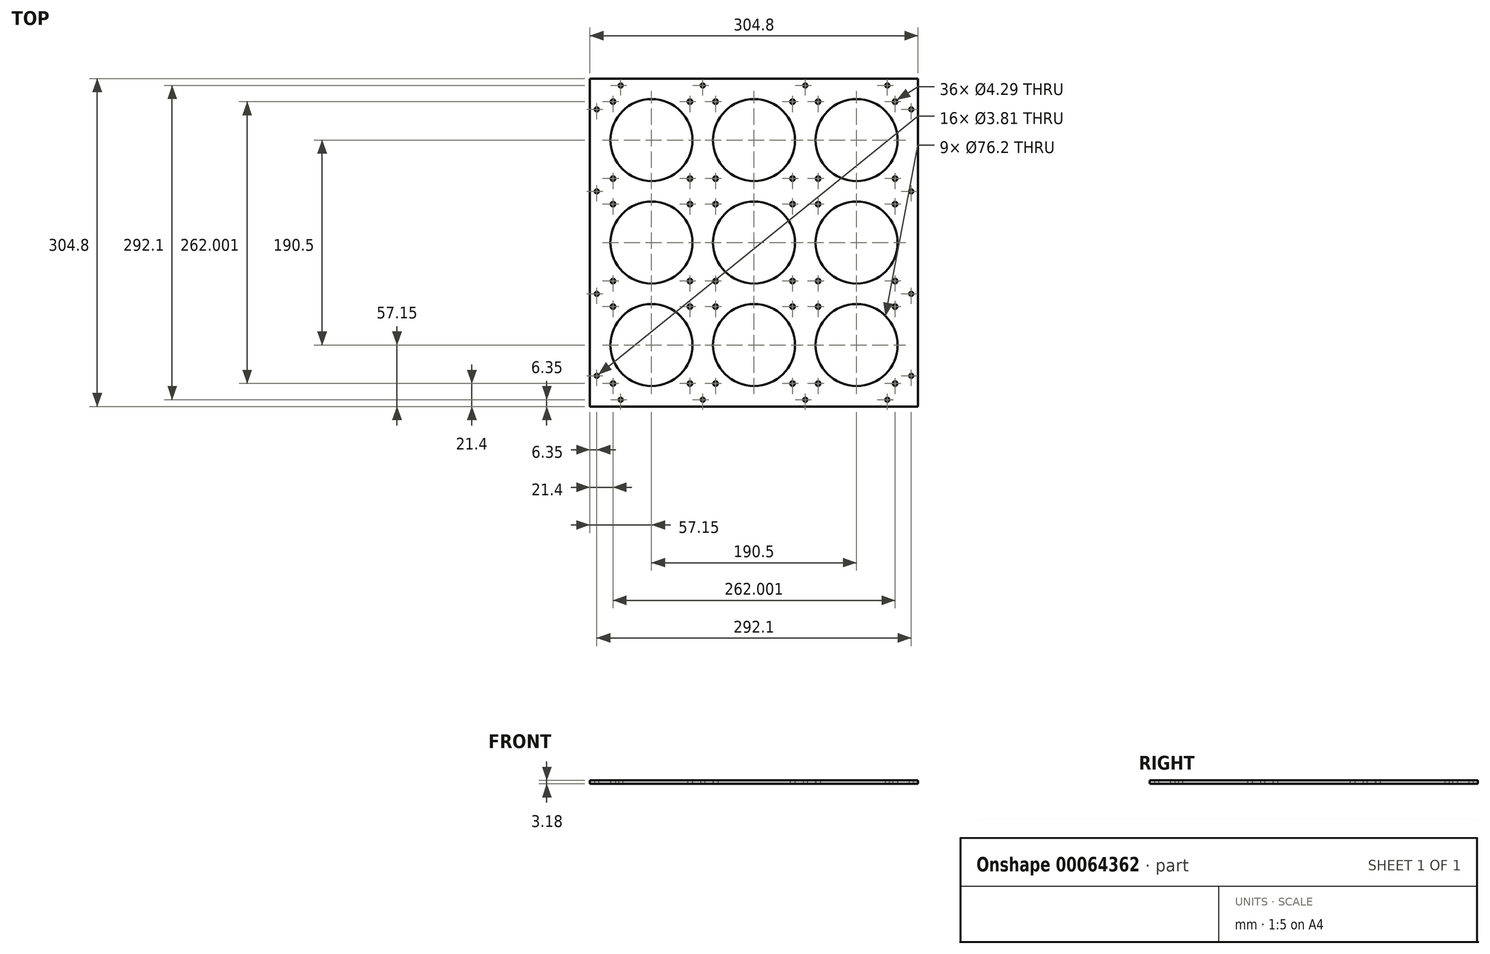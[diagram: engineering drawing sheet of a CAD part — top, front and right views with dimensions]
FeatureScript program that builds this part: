
annotation { "Feature Type Name" : "Feature", "Feature Type Description" : "" }
export const myFeature = defineFeature(function(context is Context, id is Id, definition is map)
    precondition{}
    {
        {
            var Q0;
            Q0=qCreatedBy(makeId("Top.planeOp"),FACE);
            var sketch = newSketch(context, id + "F0", { "sketchPlane" : qUnion([Q0])});
            skLineSegment(sketch, "E0.rect.bottom", {"start": v(-152.4, 152.4) * mm, "end": v(152.4, 152.4) * mm});
            skLineSegment(sketch, "E0.rect.top", {"start": v(-152.4, -152.4) * mm, "end": v(152.4, -152.4) * mm});
            skLineSegment(sketch, "E0.rect.left", {"start": v(-152.4, 152.4) * mm, "end": v(-152.4, -152.4) * mm});
            skLineSegment(sketch, "E0.rect.right", {"start": v(152.4, 152.4) * mm, "end": v(152.4, -152.4) * mm});
            skPoint(sketch, "E1", {"position": v(-47.62, 146.05) * mm});
            skPoint(sketch, "E2", {"position": v(47.63, 146.05) * mm});
            skPoint(sketch, "E3", {"position": v(-47.62, -146.05) * mm});
            skPoint(sketch, "E4", {"position": v(47.63, -146.05) * mm});
            skPoint(sketch, "E5", {"position": v(-146.05, 47.63) * mm});
            skPoint(sketch, "E6", {"position": v(-146.05, -47.62) * mm});
            skPoint(sketch, "E7", {"position": v(146.05, 47.63) * mm});
            skPoint(sketch, "E8", {"position": v(-123.83, 146.05) * mm});
            skPoint(sketch, "E9", {"position": v(-146.05, 123.83) * mm});
            skPoint(sketch, "E10", {"position": v(123.83, 146.05) * mm});
            skPoint(sketch, "E11", {"position": v(-146.05, -123.82) * mm});
            skPoint(sketch, "E12", {"position": v(-123.83, -146.05) * mm});
            skPoint(sketch, "E13", {"position": v(123.83, -146.05) * mm});
            skPoint(sketch, "E14", {"position": v(146.05, -123.82) * mm});
            skPoint(sketch, "E15", {"position": v(146.05, 123.83) * mm});
            skPoint(sketch, "E16", {"position": v(146.05, -47.62) * mm});
            skPoint(sketch, "E17.rect.middle", {"position": v(0, 0) * mm});
            skCircle(sketch, "E18", {"center": v(-95.25, 95.25) * mm, "radius": 38.1 * mm});
            skCircle(sketch, "E19", {"center": v(-131, 131) * mm, "radius": 2.15 * mm});
            skCircle(sketch, "E20.0.1.0", {"center": v(-131, 59.5) * mm, "radius": 2.15 * mm});
            skCircle(sketch, "E20.1.0.0", {"center": v(-59.5, 131) * mm, "radius": 2.15 * mm});
            skCircle(sketch, "E20.1.1.0", {"center": v(-59.5, 59.5) * mm, "radius": 2.15 * mm});
            skLineSegment(sketch, "E20.direction1", {"start": v(-131, 131) * mm, "end": v(-59.5, 131) * mm, "construction": true});
            skLineSegment(sketch, "E20.direction2", {"start": v(-131, 131) * mm, "end": v(-131, 59.5) * mm, "construction": true});
            skLineSegment(sketch, "E21.0.1.0", {"start": v(-131, 35.75) * mm, "end": v(-59.5, 35.75) * mm, "construction": true});
            skLineSegment(sketch, "E21.0.1.1", {"start": v(-131, 35.75) * mm, "end": v(-131, -35.75) * mm, "construction": true});
            skCircle(sketch, "E21.0.1.2", {"center": v(-95.25, 0) * mm, "radius": 38.1 * mm});
            skPoint(sketch, "E21.0.1.3", {"position": v(-95.25, 0) * mm});
            skCircle(sketch, "E21.0.1.4", {"center": v(-59.5, -35.75) * mm, "radius": 2.15 * mm});
            skCircle(sketch, "E21.0.1.5", {"center": v(-131, -35.75) * mm, "radius": 2.15 * mm});
            skCircle(sketch, "E21.0.1.6", {"center": v(-59.5, 35.75) * mm, "radius": 2.15 * mm});
            skCircle(sketch, "E21.0.1.7", {"center": v(-131, 35.75) * mm, "radius": 2.15 * mm});
            skLineSegment(sketch, "E21.1.0.0", {"start": v(-35.75, 131) * mm, "end": v(35.75, 131) * mm, "construction": true});
            skLineSegment(sketch, "E21.1.0.1", {"start": v(-35.75, 131) * mm, "end": v(-35.75, 59.5) * mm, "construction": true});
            skCircle(sketch, "E21.1.0.2", {"center": v(0, 95.25) * mm, "radius": 38.1 * mm});
            skPoint(sketch, "E21.1.0.3", {"position": v(0, 95.25) * mm});
            skCircle(sketch, "E21.1.0.4", {"center": v(35.75, 59.5) * mm, "radius": 2.15 * mm});
            skCircle(sketch, "E21.1.0.5", {"center": v(-35.75, 59.5) * mm, "radius": 2.15 * mm});
            skCircle(sketch, "E21.1.0.6", {"center": v(35.75, 131) * mm, "radius": 2.15 * mm});
            skCircle(sketch, "E21.1.0.7", {"center": v(-35.75, 131) * mm, "radius": 2.15 * mm});
            skLineSegment(sketch, "E21.1.1.0", {"start": v(-35.75, 35.75) * mm, "end": v(35.75, 35.75) * mm, "construction": true});
            skLineSegment(sketch, "E21.1.1.1", {"start": v(-35.75, 35.75) * mm, "end": v(-35.75, -35.75) * mm, "construction": true});
            skCircle(sketch, "E21.1.1.2", {"center": v(0, 0) * mm, "radius": 38.1 * mm});
            skCircle(sketch, "E21.1.1.4", {"center": v(35.75, -35.75) * mm, "radius": 2.15 * mm});
            skCircle(sketch, "E21.1.1.5", {"center": v(-35.75, -35.75) * mm, "radius": 2.15 * mm});
            skCircle(sketch, "E21.1.1.6", {"center": v(35.75, 35.75) * mm, "radius": 2.15 * mm});
            skCircle(sketch, "E21.1.1.7", {"center": v(-35.75, 35.75) * mm, "radius": 2.15 * mm});
            skLineSegment(sketch, "E21.2.0.0", {"start": v(59.5, 131) * mm, "end": v(131, 131) * mm, "construction": true});
            skLineSegment(sketch, "E21.2.0.1", {"start": v(59.5, 131) * mm, "end": v(59.5, 59.5) * mm, "construction": true});
            skCircle(sketch, "E21.2.0.2", {"center": v(95.25, 95.25) * mm, "radius": 38.1 * mm});
            skPoint(sketch, "E21.2.0.3", {"position": v(95.25, 95.25) * mm});
            skCircle(sketch, "E21.2.0.4", {"center": v(131, 59.5) * mm, "radius": 2.15 * mm});
            skCircle(sketch, "E21.2.0.5", {"center": v(59.5, 59.5) * mm, "radius": 2.15 * mm});
            skCircle(sketch, "E21.2.0.6", {"center": v(131, 131) * mm, "radius": 2.15 * mm});
            skCircle(sketch, "E21.2.0.7", {"center": v(59.5, 131) * mm, "radius": 2.15 * mm});
            skLineSegment(sketch, "E21.2.1.0", {"start": v(59.5, 35.75) * mm, "end": v(131, 35.75) * mm, "construction": true});
            skLineSegment(sketch, "E21.2.1.1", {"start": v(59.5, 35.75) * mm, "end": v(59.5, -35.75) * mm, "construction": true});
            skCircle(sketch, "E21.2.1.2", {"center": v(95.25, 0) * mm, "radius": 38.1 * mm});
            skPoint(sketch, "E21.2.1.3", {"position": v(95.25, 0) * mm});
            skCircle(sketch, "E21.2.1.4", {"center": v(131, -35.75) * mm, "radius": 2.15 * mm});
            skCircle(sketch, "E21.2.1.5", {"center": v(59.5, -35.75) * mm, "radius": 2.15 * mm});
            skCircle(sketch, "E21.2.1.6", {"center": v(131, 35.75) * mm, "radius": 2.15 * mm});
            skCircle(sketch, "E21.2.1.7", {"center": v(59.5, 35.75) * mm, "radius": 2.15 * mm});
            skLineSegment(sketch, "E21.direction1", {"start": v(-131, 131) * mm, "end": v(-35.75, 131) * mm, "construction": true});
            skLineSegment(sketch, "E21.direction2", {"start": v(-131, 131) * mm, "end": v(-131, 35.75) * mm, "construction": true});
            skLineSegment(sketch, "E22.0.0.2", {"start": v(-131, -59.5) * mm, "end": v(-59.5, -59.5) * mm, "construction": true});
            skLineSegment(sketch, "E22.3.0.2", {"start": v(-131, -59.5) * mm, "end": v(-131, -131) * mm, "construction": true});
            skCircle(sketch, "E22.6.0.2", {"center": v(-95.25, -95.25) * mm, "radius": 38.1 * mm});
            skPoint(sketch, "E22.8.0.2", {"position": v(-95.25, -95.25) * mm});
            skCircle(sketch, "E22.9.0.2", {"center": v(-59.5, -131) * mm, "radius": 2.15 * mm});
            skCircle(sketch, "E22.11.0.2", {"center": v(-131, -131) * mm, "radius": 2.15 * mm});
            skCircle(sketch, "E22.13.0.2", {"center": v(-59.5, -59.5) * mm, "radius": 2.15 * mm});
            skCircle(sketch, "E22.15.0.2", {"center": v(-131, -59.5) * mm, "radius": 2.15 * mm});
            skLineSegment(sketch, "E22.0.1.2", {"start": v(-35.75, -59.5) * mm, "end": v(35.75, -59.5) * mm, "construction": true});
            skLineSegment(sketch, "E22.3.1.2", {"start": v(-35.75, -59.5) * mm, "end": v(-35.75, -131) * mm, "construction": true});
            skCircle(sketch, "E22.6.1.2", {"center": v(0, -95.25) * mm, "radius": 38.1 * mm});
            skPoint(sketch, "E22.8.1.2", {"position": v(0, -95.25) * mm});
            skCircle(sketch, "E22.9.1.2", {"center": v(35.75, -131) * mm, "radius": 2.15 * mm});
            skCircle(sketch, "E22.11.1.2", {"center": v(-35.75, -131) * mm, "radius": 2.15 * mm});
            skCircle(sketch, "E22.13.1.2", {"center": v(35.75, -59.5) * mm, "radius": 2.15 * mm});
            skCircle(sketch, "E22.15.1.2", {"center": v(-35.75, -59.5) * mm, "radius": 2.15 * mm});
            skLineSegment(sketch, "E22.0.2.2", {"start": v(59.5, -59.5) * mm, "end": v(131, -59.5) * mm, "construction": true});
            skLineSegment(sketch, "E22.3.2.2", {"start": v(59.5, -59.5) * mm, "end": v(59.5, -131) * mm, "construction": true});
            skCircle(sketch, "E22.6.2.2", {"center": v(95.25, -95.25) * mm, "radius": 38.1 * mm});
            skPoint(sketch, "E22.8.2.2", {"position": v(95.25, -95.25) * mm});
            skCircle(sketch, "E22.9.2.2", {"center": v(131, -131) * mm, "radius": 2.15 * mm});
            skCircle(sketch, "E22.11.2.2", {"center": v(59.5, -131) * mm, "radius": 2.15 * mm});
            skCircle(sketch, "E22.13.2.2", {"center": v(131, -59.5) * mm, "radius": 2.15 * mm});
            skCircle(sketch, "E22.15.2.2", {"center": v(59.5, -59.5) * mm, "radius": 2.15 * mm});
            skSolve(sketch);
        }
        {
            var Q0;
            Q0=qSketchRegion(id+"F0",true);
            extrude(context, id + "F1", {"entities" : qUnion([Q0]), "depth" : 3.17 * mm});
        }
        {
            var Q0;
            Q0=sQuery(id+"F0.wireOp",VERTEX,"E9");
            var Q1;
            Q1=sQuery(id+"F0.wireOp",VERTEX,"E8");
            var Q2;
            Q2=sQuery(id+"F0.wireOp",VERTEX,"E10");
            var Q3;
            Q3=sQuery(id+"F0.wireOp",VERTEX,"E14");
            var Q4;
            Q4=sQuery(id+"F0.wireOp",VERTEX,"E13");
            var Q5;
            Q5=sQuery(id+"F0.wireOp",VERTEX,"E11");
            var Q6;
            Q6=sQuery(id+"F0.wireOp",VERTEX,"E12");
            var Q7;
            Q7=sQuery(id+"F0.wireOp",VERTEX,"E5");
            var Q8;
            Q8=sQuery(id+"F0.wireOp",VERTEX,"E6");
            var Q9;
            Q9=sQuery(id+"F0.wireOp",VERTEX,"E3");
            var Q10;
            Q10=sQuery(id+"F0.wireOp",VERTEX,"E4");
            var Q11;
            Q11=sQuery(id+"F0.wireOp",VERTEX,"E16");
            var Q12;
            Q12=sQuery(id+"F0.wireOp",VERTEX,"E7");
            var Q13;
            Q13=sQuery(id+"F0.wireOp",VERTEX,"E2");
            var Q14;
            Q14=sQuery(id+"F0.wireOp",VERTEX,"E1");
            var Q15;
            Q15=sQuery(id+"F0.wireOp",VERTEX,"E15");
            var Q16;
            Q16=makeQuery(id+"F1.opExtrude","SWEPT_BODY",BODY,{"disambiguationData":[OSD([sQuery(id+"F0.wireOp",EDGE,"E0.rect.bottom"),sQuery(id+"F0.wireOp",EDGE,"E0.rect.top"),sQuery(id+"F0.wireOp",EDGE,"E0.rect.left"),sQuery(id+"F0.wireOp",EDGE,"E0.rect.right"),sQuery(id+"F0.wireOp",EDGE,"355e2ae6-6e88-4ca4-8ebc-3fd0fd05b8a7"),sQuery(id+"F0.wireOp",EDGE,"ec92c217-216e-4417-a66e-f22207dcd941.0.1.0"),sQuery(id+"F0.wireOp",EDGE,"ec92c217-216e-4417-a66e-f22207dcd941.1.0.0"),sQuery(id+"F0.wireOp",EDGE,"ec92c217-216e-4417-a66e-f22207dcd941.1.1.0"),sQuery(id+"F0.wireOp",EDGE,"73b4038f-2a48-4c89-9a6c-eaebf8faa2ab.0.1.4"),sQuery(id+"F0.wireOp",EDGE,"73b4038f-2a48-4c89-9a6c-eaebf8faa2ab.0.1.5"),sQuery(id+"F0.wireOp",EDGE,"73b4038f-2a48-4c89-9a6c-eaebf8faa2ab.0.1.6"),sQuery(id+"F0.wireOp",EDGE,"73b4038f-2a48-4c89-9a6c-eaebf8faa2ab.0.1.7"),sQuery(id+"F0.wireOp",EDGE,"73b4038f-2a48-4c89-9a6c-eaebf8faa2ab.0.2.4"),sQuery(id+"F0.wireOp",EDGE,"73b4038f-2a48-4c89-9a6c-eaebf8faa2ab.0.2.5"),sQuery(id+"F0.wireOp",EDGE,"73b4038f-2a48-4c89-9a6c-eaebf8faa2ab.0.2.6"),sQuery(id+"F0.wireOp",EDGE,"73b4038f-2a48-4c89-9a6c-eaebf8faa2ab.0.2.7"),sQuery(id+"F0.wireOp",EDGE,"73b4038f-2a48-4c89-9a6c-eaebf8faa2ab.1.0.4"),sQuery(id+"F0.wireOp",EDGE,"73b4038f-2a48-4c89-9a6c-eaebf8faa2ab.1.0.5"),sQuery(id+"F0.wireOp",EDGE,"73b4038f-2a48-4c89-9a6c-eaebf8faa2ab.1.0.6"),sQuery(id+"F0.wireOp",EDGE,"73b4038f-2a48-4c89-9a6c-eaebf8faa2ab.1.0.7"),sQuery(id+"F0.wireOp",EDGE,"73b4038f-2a48-4c89-9a6c-eaebf8faa2ab.1.1.4"),sQuery(id+"F0.wireOp",EDGE,"73b4038f-2a48-4c89-9a6c-eaebf8faa2ab.1.1.5"),sQuery(id+"F0.wireOp",EDGE,"73b4038f-2a48-4c89-9a6c-eaebf8faa2ab.1.1.6"),sQuery(id+"F0.wireOp",EDGE,"73b4038f-2a48-4c89-9a6c-eaebf8faa2ab.1.1.7"),sQuery(id+"F0.wireOp",EDGE,"73b4038f-2a48-4c89-9a6c-eaebf8faa2ab.1.2.4"),sQuery(id+"F0.wireOp",EDGE,"73b4038f-2a48-4c89-9a6c-eaebf8faa2ab.1.2.5"),sQuery(id+"F0.wireOp",EDGE,"73b4038f-2a48-4c89-9a6c-eaebf8faa2ab.1.2.6"),sQuery(id+"F0.wireOp",EDGE,"73b4038f-2a48-4c89-9a6c-eaebf8faa2ab.1.2.7"),sQuery(id+"F0.wireOp",EDGE,"73b4038f-2a48-4c89-9a6c-eaebf8faa2ab.2.0.4"),sQuery(id+"F0.wireOp",EDGE,"73b4038f-2a48-4c89-9a6c-eaebf8faa2ab.2.0.5"),sQuery(id+"F0.wireOp",EDGE,"73b4038f-2a48-4c89-9a6c-eaebf8faa2ab.2.0.6"),sQuery(id+"F0.wireOp",EDGE,"73b4038f-2a48-4c89-9a6c-eaebf8faa2ab.2.0.7"),sQuery(id+"F0.wireOp",EDGE,"73b4038f-2a48-4c89-9a6c-eaebf8faa2ab.2.1.4"),sQuery(id+"F0.wireOp",EDGE,"73b4038f-2a48-4c89-9a6c-eaebf8faa2ab.2.1.5"),sQuery(id+"F0.wireOp",EDGE,"73b4038f-2a48-4c89-9a6c-eaebf8faa2ab.2.1.6"),sQuery(id+"F0.wireOp",EDGE,"73b4038f-2a48-4c89-9a6c-eaebf8faa2ab.2.1.7"),sQuery(id+"F0.wireOp",EDGE,"73b4038f-2a48-4c89-9a6c-eaebf8faa2ab.2.2.4"),sQuery(id+"F0.wireOp",EDGE,"73b4038f-2a48-4c89-9a6c-eaebf8faa2ab.2.2.5"),sQuery(id+"F0.wireOp",EDGE,"73b4038f-2a48-4c89-9a6c-eaebf8faa2ab.2.2.6"),sQuery(id+"F0.wireOp",EDGE,"73b4038f-2a48-4c89-9a6c-eaebf8faa2ab.2.2.7"),sQuery(id+"F0.wireOp",EDGE,"afade619-a39a-4778-b8e1-03a779a9a28b"),sQuery(id+"F0.wireOp",EDGE,"8a805056-4bb3-49c9-a1bc-3d3538aac092.0.1.0"),sQuery(id+"F0.wireOp",EDGE,"8a805056-4bb3-49c9-a1bc-3d3538aac092.0.2.0"),sQuery(id+"F0.wireOp",EDGE,"8a805056-4bb3-49c9-a1bc-3d3538aac092.1.0.0"),sQuery(id+"F0.wireOp",EDGE,"8a805056-4bb3-49c9-a1bc-3d3538aac092.1.1.0"),sQuery(id+"F0.wireOp",EDGE,"8a805056-4bb3-49c9-a1bc-3d3538aac092.1.2.0"),sQuery(id+"F0.wireOp",EDGE,"8a805056-4bb3-49c9-a1bc-3d3538aac092.2.0.0"),sQuery(id+"F0.wireOp",EDGE,"8a805056-4bb3-49c9-a1bc-3d3538aac092.2.1.0"),sQuery(id+"F0.wireOp",EDGE,"8a805056-4bb3-49c9-a1bc-3d3538aac092.2.2.0")])]});
            hole(context, id + "F2", {"style" : HoleStyle.SIMPLE, "holeDiameter" : 3.8 * mm, "endStyle" : HoleEndStyle.THROUGH, "oppositeDirection" : true, "locations" : qUnion([Q0, Q1, Q2, Q3, Q4, Q5, Q6, Q7, Q8, Q9, Q10, Q11, Q12, Q13, Q14, Q15]), "scope" : qUnion([Q16])});
        }
    });
